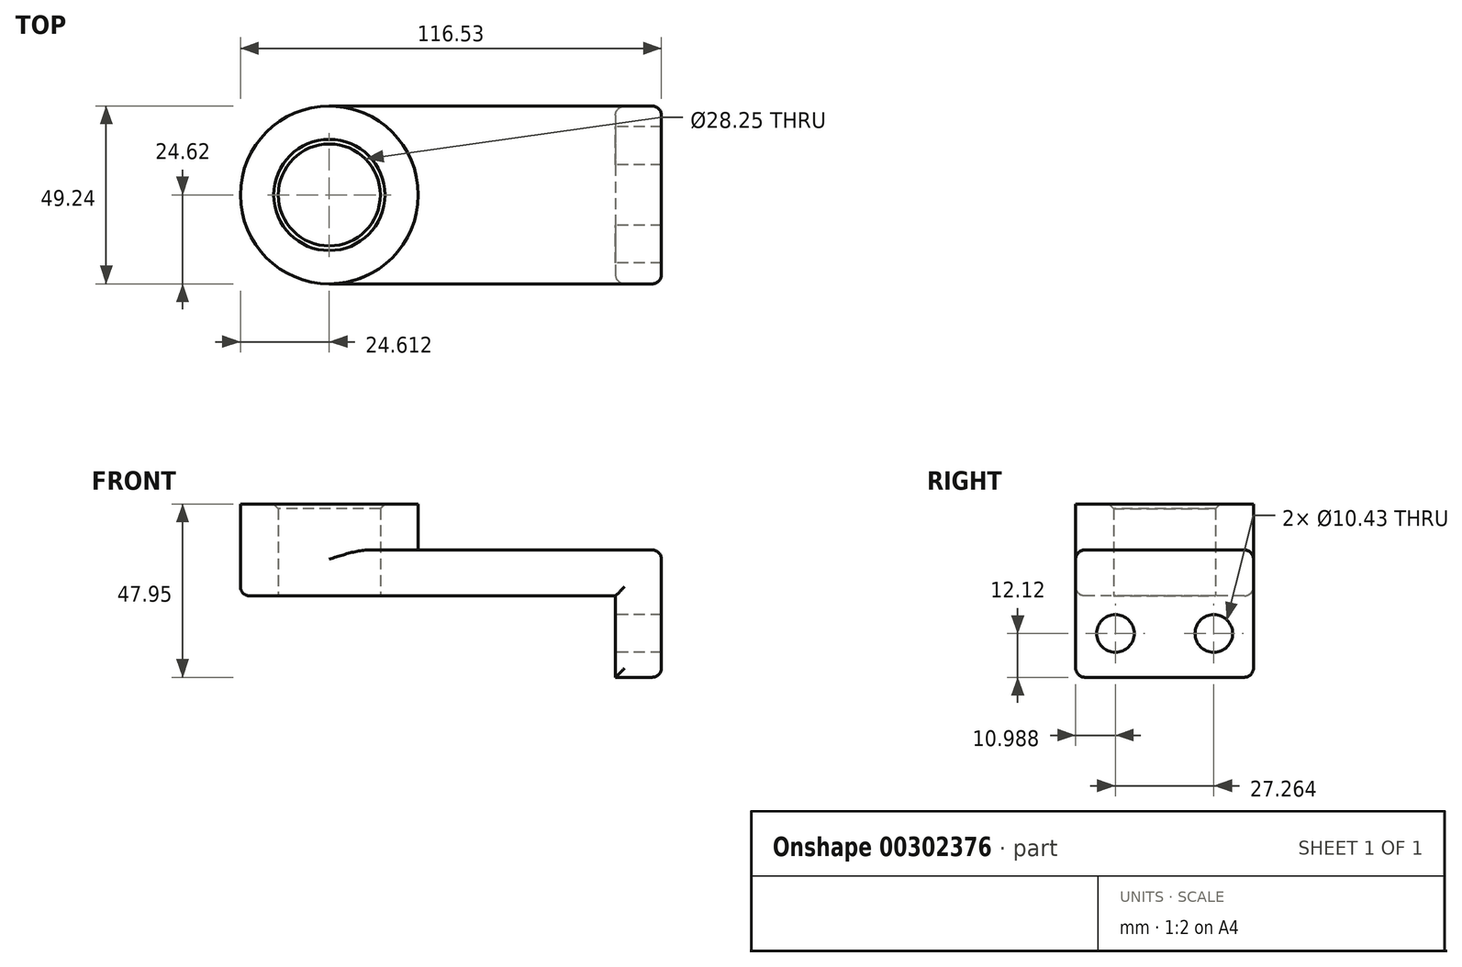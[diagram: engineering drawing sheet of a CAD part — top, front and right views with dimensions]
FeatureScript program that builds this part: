
annotation { "Feature Type Name" : "Feature", "Feature Type Description" : "" }
export const myFeature = defineFeature(function(context is Context, id is Id, definition is map)
    precondition{}
    {
        {
            var Q0;
            Q0=qCreatedBy(makeId("Top.planeOp"),FACE);
            var sketch = newSketch(context, id + "F0", { "sketchPlane" : qUnion([Q0])});
            skLineSegment(sketch, "E0.bottom", {"start": v(39.6, 24.62) * mm, "end": v(-39.6, 24.62) * mm});
            skLineSegment(sketch, "E0.top", {"start": v(39.6, -24.62) * mm, "end": v(-39.6, -24.62) * mm});
            skLineSegment(sketch, "E0.left", {"start": v(39.6, 24.62) * mm, "end": v(39.6, -24.62) * mm});
            skLineSegment(sketch, "E0.right", {"start": v(-39.6, 24.62) * mm, "end": v(-39.6, -24.62) * mm});
            skPoint(sketch, "E0.middle", {"position": v(0, 0) * mm});
            skArc(sketch, "E1", {"start": v(-39.6, 24.62) * mm, "mid": v(-64.22, 0) * mm, "end": v(-39.6, -24.62) * mm});
            skCircle(sketch, "E2", {"center": v(-39.6, 0) * mm, "radius": 14.13 * mm});
            skCircle(sketch, "E3", {"center": v(-39.6, 0) * mm, "radius": 24.62 * mm});
            skSolve(sketch);
        }
        {
            var Q0;
            {var subQ1=sQuery(id+"F0.wireOp",EDGE,"E0.right");var subQ3=sQuery(id+"F0.wireOp",EDGE,"E2");var subQ4=makeQuery(id+"F0.imprint","INTERSECT",VERTEX,{"disambiguationData":[OD(0.0)],"derivedFrom":[subQ1,subQ3]});Q0=makeQuery(id+"F0.imprint","IMPRINT",FACE,{"disambiguationData":[TD([[makeQuery(id+"F0.imprint","IMPRINT",EDGE,{"disambiguationData":[TD([[subQ4,-1.0]])],"derivedFrom":subQ3}),-1.0]])]});}
            var Q1;
            {var subQ1=sQuery(id+"F0.wireOp",EDGE,"E0.right");var subQ3=sQuery(id+"F0.wireOp",EDGE,"E2");var subQ4=makeQuery(id+"F0.imprint","INTERSECT",VERTEX,{"disambiguationData":[OD(0.0)],"derivedFrom":[subQ1,subQ3]});Q1=makeQuery(id+"F0.imprint","IMPRINT",FACE,{"disambiguationData":[TD([[makeQuery(id+"F0.imprint","IMPRINT",EDGE,{"disambiguationData":[TD([[subQ4,1.0]])],"derivedFrom":subQ3}),-1.0]])]});}
            extrude(context, id + "F1", {"entities" : qUnion([Q0, Q1]), "depth" : 25.4 * mm});
        }
        {
            var Q0;
            {var subQ0=sQuery(id+"F0.wireOp",EDGE,"E0.bottom");Q0=makeQuery(id+"F0.imprint","IMPRINT",FACE,{"disambiguationData":[TD([[makeQuery(id+"F0.imprint","IMPRINT",EDGE,{"derivedFrom":subQ0}),1.0]])]});}
            extrude(context, id + "F2", {"entities" : qUnion([Q0]), "operationType" : NewBodyOperationType.ADD, "depth" : 12.7 * mm});
        }
        {
            var Q0;
            Q0=makeQuery(id+"F2.opExtrude","SWEPT_FACE",FACE,{"disambiguationData":[OSD([sQuery(id+"F0.wireOp",EDGE,"E0.left")])]});
            var sketch = newSketch(context, id + "F3", { "sketchPlane" : qUnion([Q0])});
            skLineSegment(sketch, "E4.bottom", {"start": v(-24.62, 12.7) * mm, "end": v(24.62, 12.7) * mm});
            skLineSegment(sketch, "E4.top", {"start": v(-24.62, -22.55) * mm, "end": v(24.62, -22.55) * mm});
            skLineSegment(sketch, "E4.left", {"start": v(-24.62, 12.7) * mm, "end": v(-24.62, -22.55) * mm});
            skLineSegment(sketch, "E4.right", {"start": v(24.62, 12.7) * mm, "end": v(24.62, -22.55) * mm});
            skCircle(sketch, "E5", {"center": v(-13.63, -10.43) * mm, "radius": 5.21 * mm});
            skLineSegment(sketch, "E6", {"start": v(0, 0) * mm, "end": v(0, -26.29) * mm, "construction": true});
            skCircle(sketch, "E7.MirrorC", {"center": v(13.63, -10.43) * mm, "radius": 5.21 * mm});
            skSolve(sketch);
        }
        {
            var Q0;
            {var subQ2=sQuery(id+"F3.wireOp",EDGE,"E4.top");Q0=makeQuery(id+"F3.imprint","IMPRINT",FACE,{"disambiguationData":[TD([[makeQuery(id+"F3.imprint","IMPRINT",EDGE,{"derivedFrom":subQ2}),1.0]])]});}
            var Q1;
            {var subQ0=sQuery(id+"F3.wireOp",EDGE,"E4.bottom");Q1=makeQuery(id+"F3.imprint","IMPRINT",FACE,{"disambiguationData":[TD([[makeQuery(id+"F3.imprint","IMPRINT",EDGE,{"derivedFrom":subQ0}),1.0]])]});}
            extrude(context, id + "F4", {"entities" : qUnion([Q0, Q1]), "operationType" : NewBodyOperationType.ADD, "depth" : 12.7 * mm});
        }
        {
            var Q0;
            Q0=makeQuery(id+"F4.boolean.opBoolean","MERGE",FACE,{"derivedFrom":[makeQuery(id+"F2.opExtrude","SWEPT_FACE",FACE,{"disambiguationData":[OSD([sQuery(id+"F0.wireOp",EDGE,"E0.top")])]}),makeQuery(id+"F4.opExtrude","SWEPT_FACE",FACE,{"disambiguationData":[OSD([sQuery(id+"F3.wireOp",EDGE,"E4.left")])]})]});
            var Q1;
            Q1=makeQuery(id+"F4.boolean.opBoolean","MERGE",FACE,{"derivedFrom":[makeQuery(id+"F2.opExtrude","SWEPT_FACE",FACE,{"disambiguationData":[OSD([sQuery(id+"F0.wireOp",EDGE,"E0.bottom")])]}),makeQuery(id+"F4.opExtrude","SWEPT_FACE",FACE,{"disambiguationData":[OSD([sQuery(id+"F3.wireOp",EDGE,"E4.right")])]})]});
            var Q2;
            Q2=makeQuery(id+"F4.opExtrude","CAP_EDGE",EDGE,{"disambiguationData":[OSD([sQuery(id+"F3.wireOp",EDGE,"E4.bottom")])],"isStart":false});
            var Q3;
            Q3=makeQuery(id+"F4.opExtrude","CAP_EDGE",EDGE,{"disambiguationData":[OSD([sQuery(id+"F3.wireOp",EDGE,"E4.top")])],"isStart":false});
            fillet(context, id + "F5", {"entities" : qUnion([Q0, Q1, Q2, Q3]), "radius" : 2.54 * mm, "tangentPropagation" : true, "allowEdgeOverflow" : false});
        }
        {
            var Q0;
            Q0=makeQuery(id+"F1.opExtrude","CAP_EDGE",EDGE,{"disambiguationData":[OSD([sQuery(id+"F0.wireOp",EDGE,"E2")])],"isStart":false});
            var Q1;
            Q1=makeQuery(id+"F2.opExtrude","CAP_EDGE",EDGE,{"disambiguationData":[OSD([sQuery(id+"F0.wireOp",EDGE,"E3")])],"isStart":false});
            chamfer(context, id + "F6", {"entities" : qUnion([Q0, Q1]), "width" : 1.27 * mm, "tangentPropagation" : true});
        }
    });
